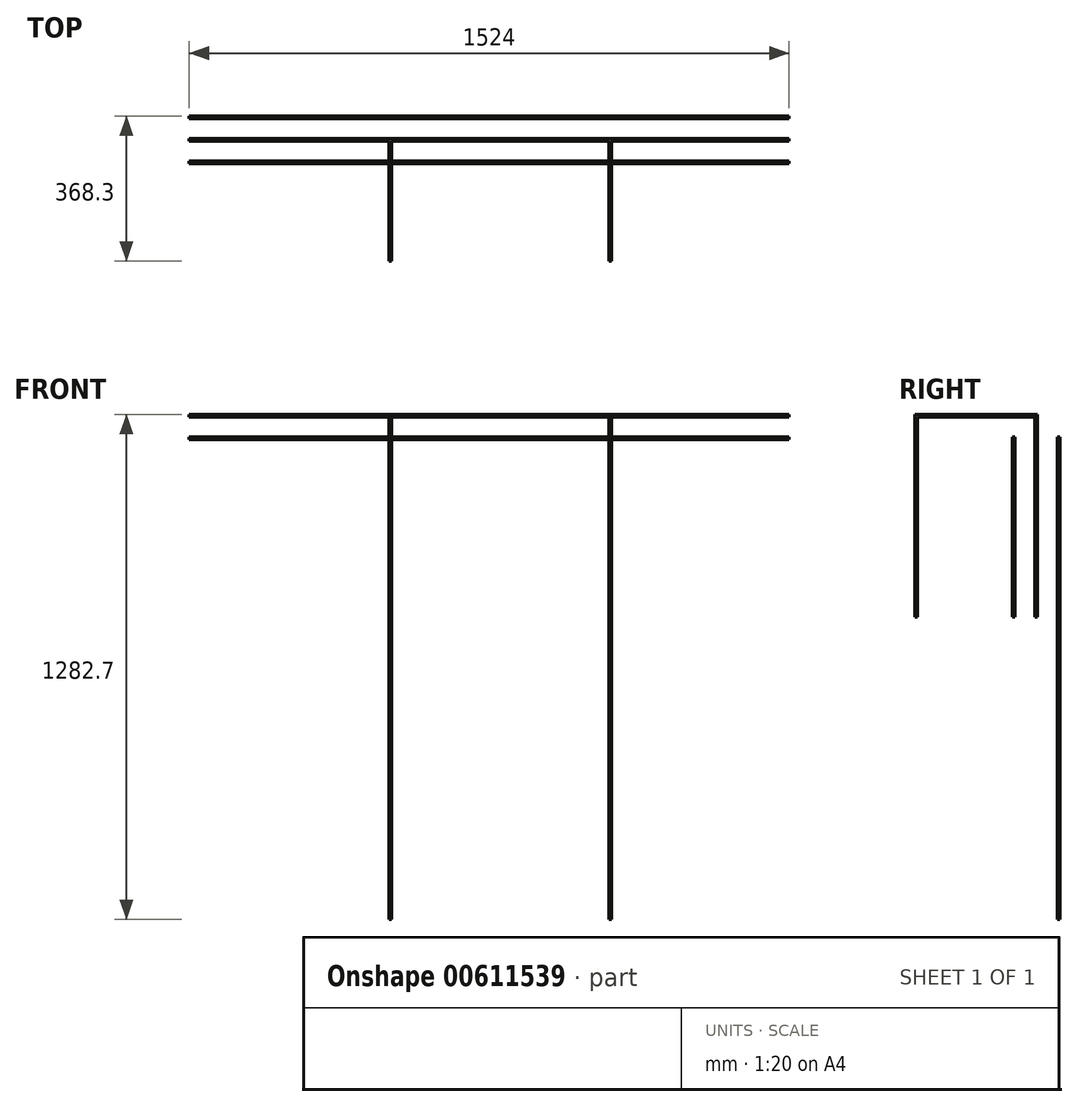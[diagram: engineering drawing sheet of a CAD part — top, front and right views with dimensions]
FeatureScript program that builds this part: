
annotation { "Feature Type Name" : "Feature", "Feature Type Description" : "" }
export const myFeature = defineFeature(function(context is Context, id is Id, definition is map)
    precondition{}
    {
        {
            var Q0;
            Q0=qCreatedBy(makeId("Right.planeOp"),FACE);
            var sketch = newSketch(context, id + "F0", { "sketchPlane" : qUnion([Q0])});
            skLineSegment(sketch, "E0.bottom", {"start": v(0, 0) * mm, "end": v(-6.35, 0) * mm});
            skLineSegment(sketch, "E0.top", {"start": v(0, -6.35) * mm, "end": v(-6.35, -6.35) * mm});
            skLineSegment(sketch, "E0.left", {"start": v(0, 0) * mm, "end": v(0, -6.35) * mm});
            skLineSegment(sketch, "E0.right", {"start": v(-6.35, 0) * mm, "end": v(-6.35, -6.35) * mm});
            skSolve(sketch);
        }
        {
            var Q0;
            Q0 = qSketchRegion(id + "F0", true);
            extrude(context, id + "F1", {"entities" : qUnion([Q0]), "depth" : 1524 * mm, "offsetDistance" : 25.4 * mm});
        }
        {
            var Q0;
            Q0=makeQuery(id+"F1.opExtrude","SWEPT_FACE",FACE,{"disambiguationData":[OSD([sQuery(id+"F0.wireOp",EDGE,"E0.top")])]});
            var sketch = newSketch(context, id + "F2", { "sketchPlane" : qUnion([Q0])});
            skLineSegment(sketch, "E1.bottom", {"start": v(508, 6.35) * mm, "end": v(514.35, 6.35) * mm});
            skLineSegment(sketch, "E1.top", {"start": v(508, 0) * mm, "end": v(514.35, 0) * mm});
            skLineSegment(sketch, "E1.left", {"start": v(508, 6.35) * mm, "end": v(508, 0) * mm});
            skLineSegment(sketch, "E1.right", {"start": v(514.35, 6.35) * mm, "end": v(514.35, 0) * mm});
            skLineSegment(sketch, "E2.bottom", {"start": v(1066.8, 6.35) * mm, "end": v(1073.15, 6.35) * mm});
            skLineSegment(sketch, "E2.top", {"start": v(1066.8, 0) * mm, "end": v(1073.15, 0) * mm});
            skLineSegment(sketch, "E2.left", {"start": v(1066.8, 6.35) * mm, "end": v(1066.8, 0) * mm});
            skLineSegment(sketch, "E2.right", {"start": v(1073.15, 6.35) * mm, "end": v(1073.15, 0) * mm});
            skSolve(sketch);
        }
        {
            var Q0;
            Q0 = qSketchRegion(id + "F2", true);
            extrude(context, id + "F3", {"entities" : qUnion([Q0]), "operationType" : NewBodyOperationType.ADD, "depth" : 508 * mm, "offsetDistance" : 25.4 * mm});
        }
        {
            var Q0;
            Q0=makeQuery(id+"F3.boolean.opBoolean","MERGE",FACE,{"derivedFrom":[makeQuery(id+"F1.opExtrude","SWEPT_FACE",FACE,{"disambiguationData":[OSD([sQuery(id+"F0.wireOp",EDGE,"E0.right")])]}),makeQuery(id+"F3.opExtrude","SWEPT_FACE",FACE,{"disambiguationData":[OSD([sQuery(id+"F2.wireOp",EDGE,"E1.bottom")])]}),makeQuery(id+"F3.opExtrude","SWEPT_FACE",FACE,{"disambiguationData":[OSD([sQuery(id+"F2.wireOp",EDGE,"E2.bottom")])]})]});
            var sketch = newSketch(context, id + "F4", { "sketchPlane" : qUnion([Q0])});
            skLineSegment(sketch, "E3.bottom", {"start": v(508, 0) * mm, "end": v(514.35, 0) * mm});
            skLineSegment(sketch, "E3.top", {"start": v(508, -6.35) * mm, "end": v(514.35, -6.35) * mm});
            skLineSegment(sketch, "E3.left", {"start": v(508, 0) * mm, "end": v(508, -6.35) * mm});
            skLineSegment(sketch, "E3.right", {"start": v(514.35, 0) * mm, "end": v(514.35, -6.35) * mm});
            skLineSegment(sketch, "E4.bottom", {"start": v(1066.8, 0) * mm, "end": v(1073.15, 0) * mm});
            skLineSegment(sketch, "E4.top", {"start": v(1066.8, -6.35) * mm, "end": v(1073.15, -6.35) * mm});
            skLineSegment(sketch, "E4.left", {"start": v(1066.8, 0) * mm, "end": v(1066.8, -6.35) * mm});
            skLineSegment(sketch, "E4.right", {"start": v(1073.15, 0) * mm, "end": v(1073.15, -6.35) * mm});
            skSolve(sketch);
        }
        {
            var Q0;
            Q0 = qSketchRegion(id + "F4", true);
            extrude(context, id + "F5", {"entities" : qUnion([Q0]), "operationType" : NewBodyOperationType.ADD, "depth" : 304.8 * mm, "offsetDistance" : 25.4 * mm});
        }
        {
            var Q0;
            Q0=makeQuery(id+"F5.opExtrude","SWEPT_FACE",FACE,{"disambiguationData":[OSD([sQuery(id+"F4.wireOp",EDGE,"E3.top")])]});
            var sketch = newSketch(context, id + "F6", { "sketchPlane" : qUnion([Q0])});
            skLineSegment(sketch, "E5.bottom", {"start": v(508, 311.15) * mm, "end": v(514.35, 311.15) * mm});
            skLineSegment(sketch, "E5.top", {"start": v(508, 304.8) * mm, "end": v(514.35, 304.8) * mm});
            skLineSegment(sketch, "E5.left", {"start": v(508, 311.15) * mm, "end": v(508, 304.8) * mm});
            skLineSegment(sketch, "E5.right", {"start": v(514.35, 311.15) * mm, "end": v(514.35, 304.8) * mm});
            skLineSegment(sketch, "E6.bottom", {"start": v(1073.15, 311.15) * mm, "end": v(1066.8, 311.15) * mm});
            skLineSegment(sketch, "E6.top", {"start": v(1073.15, 304.8) * mm, "end": v(1066.8, 304.8) * mm});
            skLineSegment(sketch, "E6.left", {"start": v(1073.15, 311.15) * mm, "end": v(1073.15, 304.8) * mm});
            skLineSegment(sketch, "E6.right", {"start": v(1066.8, 311.15) * mm, "end": v(1066.8, 304.8) * mm});
            skSolve(sketch);
        }
        {
            var Q0;
            Q0 = qSketchRegion(id + "F6", true);
            var Q1;
            Q1=makeQuery(id+"F3.opExtrude","CAP_FACE",FACE,{"disambiguationData":[OSD([sQuery(id+"F2.wireOp",EDGE,"E1.bottom"),sQuery(id+"F2.wireOp",EDGE,"E1.top"),sQuery(id+"F2.wireOp",EDGE,"E1.left"),sQuery(id+"F2.wireOp",EDGE,"E1.right")])],"isStart":false});
            extrude(context, id + "F7", {"entities" : qUnion([Q0]), "operationType" : NewBodyOperationType.ADD, "endBound" : BoundingType.UP_TO_SURFACE, "depth" : 25.4 * mm, "endBoundEntityFace" : qUnion([Q1]), "offsetDistance" : 25.4 * mm});
        }
        {
            var Q0;
            Q0=qCreatedBy(makeId("Right.planeOp"),FACE);
            var sketch = newSketch(context, id + "F8", { "sketchPlane" : qUnion([Q0])});
            skLineSegment(sketch, "E7.bottom", {"start": v(-57.15, -57.15) * mm, "end": v(-63.5, -57.15) * mm});
            skLineSegment(sketch, "E7.top", {"start": v(-57.15, -63.5) * mm, "end": v(-63.5, -63.5) * mm});
            skLineSegment(sketch, "E7.left", {"start": v(-57.15, -57.15) * mm, "end": v(-57.15, -63.5) * mm});
            skLineSegment(sketch, "E7.right", {"start": v(-63.5, -57.15) * mm, "end": v(-63.5, -63.5) * mm});
            skSolve(sketch);
        }
        {
            var Q0;
            Q0 = qSketchRegion(id + "F8", true);
            var Q1;
            Q1=makeQuery(id+"F1.opExtrude","CAP_FACE",FACE,{"disambiguationData":[OSD([sQuery(id+"F0.wireOp",EDGE,"E0.bottom"),sQuery(id+"F0.wireOp",EDGE,"E0.top"),sQuery(id+"F0.wireOp",EDGE,"E0.left"),sQuery(id+"F0.wireOp",EDGE,"E0.right")])],"isStart":false});
            extrude(context, id + "F9", {"entities" : qUnion([Q0]), "endBound" : BoundingType.UP_TO_SURFACE, "depth" : 25.4 * mm, "endBoundEntityFace" : qUnion([Q1]), "offsetDistance" : 25.4 * mm});
        }
        {
            var Q0;
            Q0=makeQuery(id+"F9.opExtrude","SWEPT_FACE",FACE,{"disambiguationData":[OSD([sQuery(id+"F8.wireOp",EDGE,"E7.top")])]});
            var sketch = newSketch(context, id + "F10", { "sketchPlane" : qUnion([Q0])});
            skLineSegment(sketch, "E8.bottom", {"start": v(508, 63.5) * mm, "end": v(514.35, 63.5) * mm});
            skLineSegment(sketch, "E8.top", {"start": v(508, 57.15) * mm, "end": v(514.35, 57.15) * mm});
            skLineSegment(sketch, "E8.left", {"start": v(508, 63.5) * mm, "end": v(508, 57.15) * mm});
            skLineSegment(sketch, "E8.right", {"start": v(514.35, 63.5) * mm, "end": v(514.35, 57.15) * mm});
            skSolve(sketch);
        }
        {
            var Q0;
            Q0 = qSketchRegion(id + "F10", true);
            var Q1;
            Q1=makeQuery(id+"F3.opExtrude","CAP_FACE",FACE,{"disambiguationData":[OSD([sQuery(id+"F2.wireOp",EDGE,"E1.bottom"),sQuery(id+"F2.wireOp",EDGE,"E1.top"),sQuery(id+"F2.wireOp",EDGE,"E1.left"),sQuery(id+"F2.wireOp",EDGE,"E1.right")])],"isStart":false});
            extrude(context, id + "F11", {"entities" : qUnion([Q0]), "operationType" : NewBodyOperationType.ADD, "endBound" : BoundingType.UP_TO_SURFACE, "depth" : 25.4 * mm, "endBoundEntityFace" : qUnion([Q1]), "offsetDistance" : 25.4 * mm});
        }
        {
            var Q0;
            Q0=qCreatedBy(makeId("Right.planeOp"),FACE);
            var sketch = newSketch(context, id + "F12", { "sketchPlane" : qUnion([Q0])});
            skLineSegment(sketch, "E9.bottom", {"start": v(57.15, -57.15) * mm, "end": v(50.8, -57.15) * mm});
            skLineSegment(sketch, "E9.top", {"start": v(57.15, -63.5) * mm, "end": v(50.8, -63.5) * mm});
            skLineSegment(sketch, "E9.left", {"start": v(57.15, -57.15) * mm, "end": v(57.15, -63.5) * mm});
            skLineSegment(sketch, "E9.right", {"start": v(50.8, -57.15) * mm, "end": v(50.8, -63.5) * mm});
            skSolve(sketch);
        }
        {
            var Q0;
            Q0 = qSketchRegion(id + "F12", true);
            var Q1;
            Q1=makeQuery(id+"F9.opExtrude","CAP_FACE",FACE,{"disambiguationData":[OSD([sQuery(id+"F8.wireOp",EDGE,"E7.bottom"),sQuery(id+"F8.wireOp",EDGE,"E7.top"),sQuery(id+"F8.wireOp",EDGE,"E7.left"),sQuery(id+"F8.wireOp",EDGE,"E7.right")])],"isStart":false});
            extrude(context, id + "F13", {"entities" : qUnion([Q0]), "endBound" : BoundingType.UP_TO_SURFACE, "depth" : 25.4 * mm, "endBoundEntityFace" : qUnion([Q1]), "offsetDistance" : 25.4 * mm});
        }
        {
            var Q0;
            Q0=makeQuery(id+"F13.opExtrude","SWEPT_FACE",FACE,{"disambiguationData":[OSD([sQuery(id+"F12.wireOp",EDGE,"E9.top")])]});
            var sketch = newSketch(context, id + "F14", { "sketchPlane" : qUnion([Q0])});
            skLineSegment(sketch, "E10.bottom", {"start": v(508, -50.8) * mm, "end": v(514.35, -50.8) * mm});
            skLineSegment(sketch, "E10.top", {"start": v(508, -57.15) * mm, "end": v(514.35, -57.15) * mm});
            skLineSegment(sketch, "E10.left", {"start": v(508, -50.8) * mm, "end": v(508, -57.15) * mm});
            skLineSegment(sketch, "E10.right", {"start": v(514.35, -50.8) * mm, "end": v(514.35, -57.15) * mm});
            skLineSegment(sketch, "E11.bottom", {"start": v(1066.8, -50.8) * mm, "end": v(1073.15, -50.8) * mm});
            skLineSegment(sketch, "E11.top", {"start": v(1066.8, -57.15) * mm, "end": v(1073.15, -57.15) * mm});
            skLineSegment(sketch, "E11.left", {"start": v(1066.8, -50.8) * mm, "end": v(1066.8, -57.15) * mm});
            skLineSegment(sketch, "E11.right", {"start": v(1073.15, -50.8) * mm, "end": v(1073.15, -57.15) * mm});
            skSolve(sketch);
        }
        {
            var Q0;
            Q0 = qSketchRegion(id + "F14", true);
            extrude(context, id + "F15", {"entities" : qUnion([Q0]), "operationType" : NewBodyOperationType.ADD, "depth" : 1219.2 * mm, "offsetDistance" : 25.4 * mm});
        }
    });
